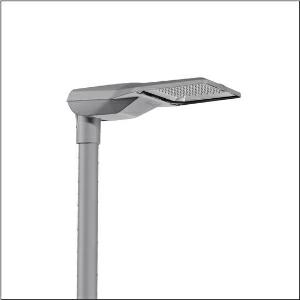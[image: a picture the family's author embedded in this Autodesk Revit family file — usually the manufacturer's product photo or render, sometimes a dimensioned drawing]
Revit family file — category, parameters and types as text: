
# Revit family: streetlight_sl_21_iq_midi___st1_0a_5xe3d21d08nb_d513
name_source: partatom
category: Lighting Fixtures
units: mm (PartAtom-declared; Revit-internal decimal feet)

## family parameters
Cut with Voids When Loaded = No
Host = Face
Light Source = No
Part Type = Normal
Room Calculation Point = No
Round Connector Dimension = Use Diameter
Shared = No

## types (1)
- --- (1 x LED, 19210 lm, 155.5 W, 2200K)
    Apparent Load = 155 VA
    CIE Flux Codes = 40 73 97 100 100
    Color Rendering = 70
    Color Temperature = 2200K
    Default Elevation = 1800 mm
    Description = Streetlight SL 21 iQ midi, mast luminaire, primary light control with lens, of PMMA, primary optical cover: cover, of toughened safety glass, transparent, light distribution: ST1.0a, light emission: direct distribution, primary light characteristic: asymmetric, installation type: post-top, side-entry, LED, High Power LED, rated luminous flux: 19.210lm, luminous efficacy: 124lm/W, light colour: 722, colour temperature: 2200K, control: Auto-Match, Temp-Guard, Lumen-Switch, Night-Set, Smart-Wire, Light-Fading, Desk-Remote (wireless, voltage-free reading and setting of iQ features in the workshop via application-optimized NFC function/RFID function), optimised constant luminous flux control (CLO 2.0), pre-setting: linear dimming characteristic, mains connection: 230..240V, AC, 50/60Hz, start of lifetime: 156W, end of service life: 162W, reduction: 69W, luminaire housing, of diecast aluminium, powder-coated, Siteco® metallic grey (DB 702S), corrosivity category C5 mid according to DIN EN ISO 12944, please order mast flange separately, inclination adjustable: 0°, 5°, 10°, 15°, sealing non-destructively replaceable, multi-level sealing system, length: 644mm, width: 335mm, height: 110mm, mast flange for spigot size: 42mm (side-entry): 5XC10008XM4, 60/48mm (side-entry/post-top): 5XC10108XM2, 76/60mm (side-entry/post-top): 5XC10108XM1, protection rating (complete): IP66, insulation class (complete): insulation class II (safety insulation), certification: CE, ENEC, ENEC+, VDE, impact resistance: IK09, permissible operating ambient temperature for outdoor applications: -40..+50°C, standard-compliant lighting for roads and squares, packaging unit: 1 piece

Light Distribution: ST1.0a
    Height = 111 mm
    Lamp = 1 x LED
    Lamp Light Flux = 19210 lm
    Lamp Power = 155.5 W
    Lamp count = 1
    Length = 644 mm
    Luminous efficacy = 124 lm/W
    Manufacturer = Siteco
    ModVariant = No
    Model = 5XE3D21D08NB
    Number of Poles = 1
    OnlyDefault = Yes
    Power Factor = 1
    Product Name = Streetlight SL 21 iQ midi | ST1.0a
    Product group = mast luminaire | pylon top
    ProductGroupID = 6100
    Protection Class = Protection class II
    Protection Degree = IP 66
    RLX_Detail_Level = 1
    RLX_Emergency_Light_Flux = 0 lm
    RLX_Emergency_Type = 0
    RLX_Emergency_Type_DB = No
    RlxData = <blob elided: 90973 chars, md5=fbde46d3>
    Socket = socket
    Standby Power = 0 W
    System Light Flux = 19210 lm
    System Power = 155 W
    Type Comments = factory setting: luminous flux: 100 % | dim-lin: 254 | 823 mA
    Type Image = l_1004298.jpg
    URL = http://relux.com
    VarID = @adj_141737
    Voltage = 0 V
    Weight = 0.00 kg
    Width = 336 mm

## geometry (parser evidence)
native form markers: Blend x4, Sweep x13
no freeform markers — native parametric forms only
